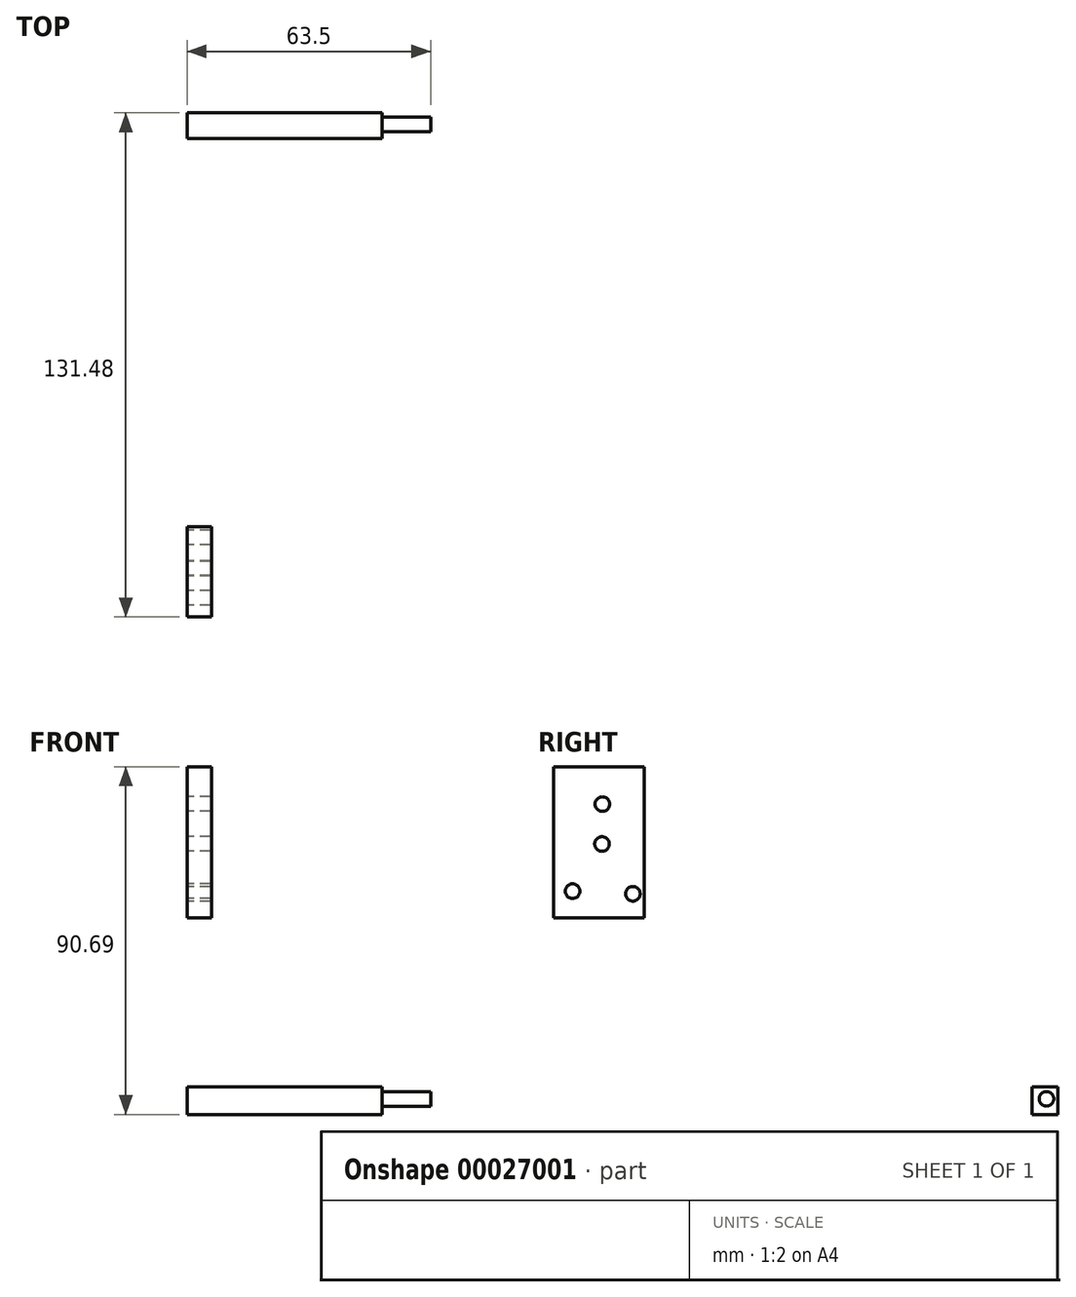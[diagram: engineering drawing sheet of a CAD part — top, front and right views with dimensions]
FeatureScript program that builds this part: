
annotation { "Feature Type Name" : "Feature", "Feature Type Description" : "" }
export const myFeature = defineFeature(function(context is Context, id is Id, definition is map)
    precondition{}
    {
        {
            var Q0;
            Q0=qCreatedBy(makeId("Right.planeOp"),FACE);
            var sketch = newSketch(context, id + "F0", { "sketchPlane" : qUnion([Q0])});
            skLineSegment(sketch, "E0.rect.bottom", {"start": v(-81.87, 36.63) * mm, "end": v(-105.46, 36.63) * mm});
            skLineSegment(sketch, "E0.rect.top", {"start": v(-81.87, 76.05) * mm, "end": v(-105.46, 76.05) * mm});
            skLineSegment(sketch, "E0.rect.left", {"start": v(-81.87, 36.63) * mm, "end": v(-81.87, 76.05) * mm});
            skLineSegment(sketch, "E0.rect.right", {"start": v(-105.46, 36.63) * mm, "end": v(-105.46, 76.05) * mm});
            skPoint(sketch, "E0.rect.middle", {"position": v(-93.66, 56.34) * mm});
            skLineSegment(sketch, "E1", {"start": v(33.82, 26.48) * mm, "end": v(33.82, 15.32) * mm});
            skLineSegment(sketch, "E2", {"start": v(33.82, 15.32) * mm, "end": v(43.22, 15.32) * mm});
            skLineSegment(sketch, "E3", {"start": v(43.22, 15.32) * mm, "end": v(43.22, 23.5) * mm});
            skLineSegment(sketch, "E4", {"start": v(43.22, 23.5) * mm, "end": v(33.82, 26.48) * mm});
            skLineSegment(sketch, "E5.rect.bottom", {"start": v(26.02, -14.64) * mm, "end": v(19.34, -14.64) * mm});
            skLineSegment(sketch, "E5.rect.top", {"start": v(26.02, -7.44) * mm, "end": v(19.34, -7.44) * mm});
            skLineSegment(sketch, "E5.rect.left", {"start": v(26.02, -14.64) * mm, "end": v(26.02, -7.44) * mm});
            skLineSegment(sketch, "E5.rect.right", {"start": v(19.34, -14.64) * mm, "end": v(19.34, -7.44) * mm});
            skPoint(sketch, "E5.rect.middle", {"position": v(22.68, -11.04) * mm});
            skSolve(sketch);
        }
        {
            var Q0;
            Q0=makeQuery(id+"F0.imprint","IMPRINT",FACE,{"disambiguationData":[TD([[makeQuery(id+"F0.imprint","IMPRINT",EDGE,{"derivedFrom":sQuery(id+"F0.wireOp",EDGE,"E0.rect.bottom")}),-1.0]])]});
            extrude(context, id + "F1", {"entities" : qUnion([Q0]), "depth" : 6.35 * mm});
        }
        {
            var Q0;
            Q0=makeQuery(id+"F0.imprint","IMPRINT",FACE,{"disambiguationData":[TD([[makeQuery(id+"F0.imprint","IMPRINT",EDGE,{"derivedFrom":sQuery(id+"F0.wireOp",EDGE,"E5.rect.bottom")}),-1.0]])]});
            extrude(context, id + "F2", {"entities" : qUnion([Q0]), "depth" : 50.8 * mm});
        }
        {
            var Q0;
            Q0=makeQuery(id+"F1.opExtrude","CAP_FACE",FACE,{"disambiguationData":[OSD([sQuery(id+"F0.wireOp",EDGE,"E0.rect.bottom"),sQuery(id+"F0.wireOp",EDGE,"E0.rect.top"),sQuery(id+"F0.wireOp",EDGE,"E0.rect.left"),sQuery(id+"F0.wireOp",EDGE,"E0.rect.right")])],"isStart":true});
            var sketch = newSketch(context, id + "F3", { "sketchPlane" : qUnion([Q0])});
            skCircle(sketch, "E6", {"center": v(92.72, 66.28) * mm, "radius": 1.9 * mm});
            skCircle(sketch, "E7", {"center": v(92.83, 55.88) * mm, "radius": 1.9 * mm});
            skCircle(sketch, "E8", {"center": v(100.49, 43.58) * mm, "radius": 1.9 * mm});
            skCircle(sketch, "E9", {"center": v(84.76, 42.89) * mm, "radius": 1.9 * mm});
            skSolve(sketch);
        }
        {
            var Q0;
            Q0 = qSketchRegion(id + "F3", true);
            extrude(context, id + "F4", {"entities" : qUnion([Q0]), "operationType" : NewBodyOperationType.REMOVE, "oppositeDirection" : true, "depth" : 7.48 * mm});
        }
        {
            var Q0;
            Q0=makeQuery(id+"F2.opExtrude","CAP_FACE",FACE,{"disambiguationData":[OSD([sQuery(id+"F0.wireOp",EDGE,"E5.rect.bottom"),sQuery(id+"F0.wireOp",EDGE,"E5.rect.top"),sQuery(id+"F0.wireOp",EDGE,"E5.rect.left"),sQuery(id+"F0.wireOp",EDGE,"E5.rect.right")])],"isStart":false});
            var sketch = newSketch(context, id + "F5", { "sketchPlane" : qUnion([Q0])});
            skCircle(sketch, "E10", {"center": v(23.04, -10.56) * mm, "radius": 1.9 * mm});
            skSolve(sketch);
        }
        {
            var Q0;
            Q0 = qSketchRegion(id + "F5", true);
            extrude(context, id + "F6", {"entities" : qUnion([Q0]), "operationType" : NewBodyOperationType.ADD, "depth" : 12.7 * mm});
        }
    });
